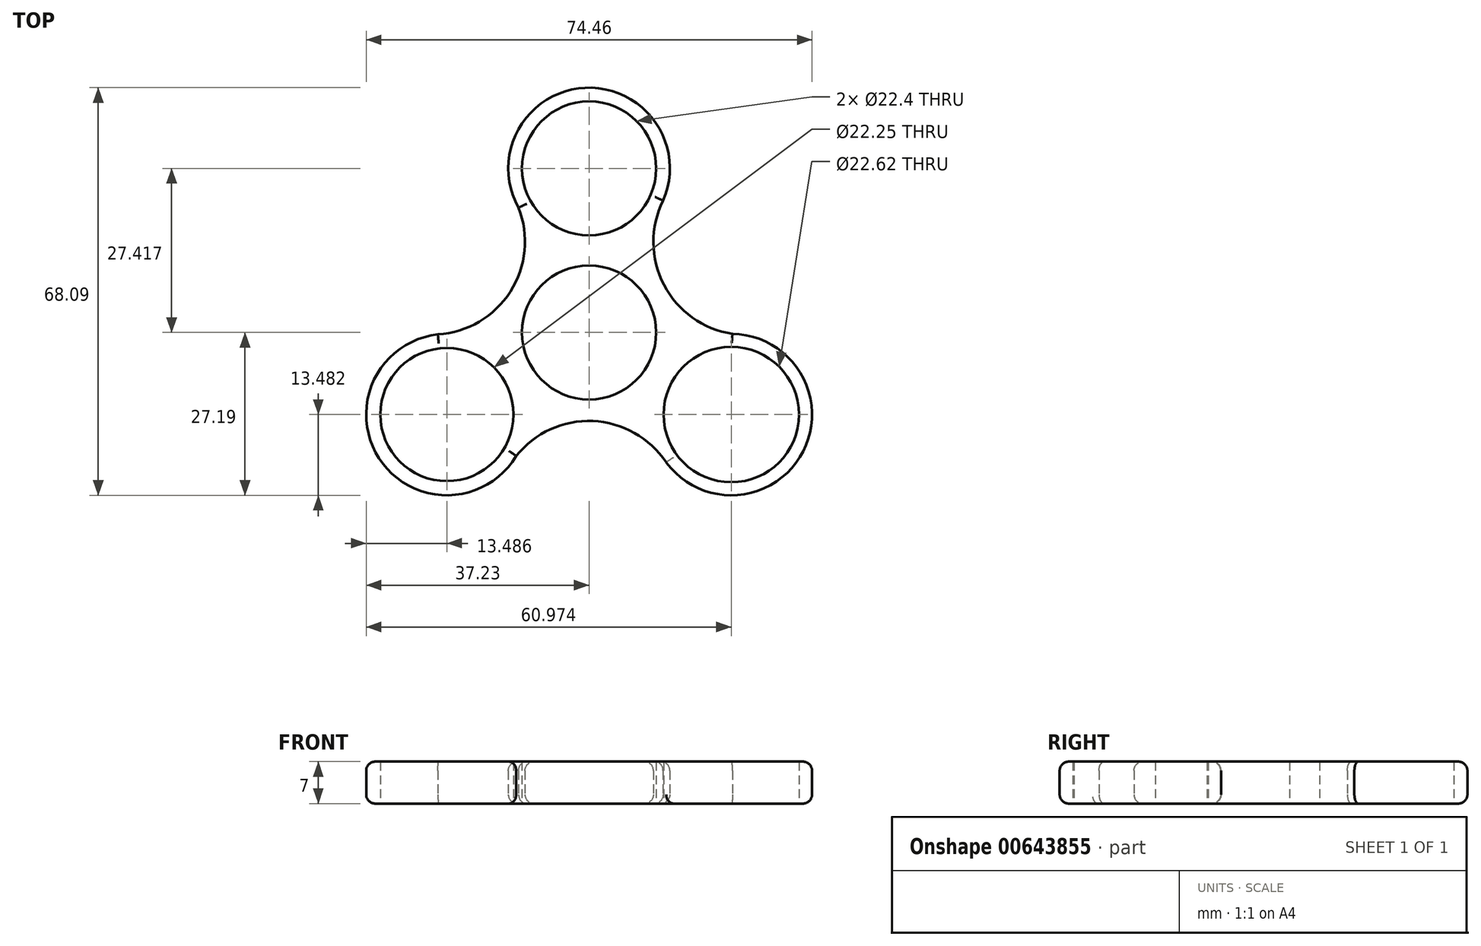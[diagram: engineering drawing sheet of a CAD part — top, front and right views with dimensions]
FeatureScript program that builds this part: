
annotation { "Feature Type Name" : "Feature", "Feature Type Description" : "" }
export const myFeature = defineFeature(function(context is Context, id is Id, definition is map)
    precondition{}
    {
        {
            var Q0;
            Q0=qCreatedBy(makeId("Top.planeOp"),FACE);
            var sketch = newSketch(context, id + "F0", { "sketchPlane" : qUnion([Q0])});
            skCircle(sketch, "E0", {"center": v(0, 0) * mm, "radius": 11.2 * mm});
            skCircle(sketch, "E1", {"center": v(0, 27.42) * mm, "radius": 11.2 * mm});
            skArc(sketch, "E2", {"start": v(12.06, 21.4) * mm, "mid": v(-0.3, 40.9) * mm, "end": v(-11.78, 20.85) * mm});
            skArc(sketch, "E3.1.0", {"start": v(-24.56, -0.25) * mm, "mid": v(-35.26, -20.71) * mm, "end": v(-12.17, -20.62) * mm});
            skArc(sketch, "E3.2.0", {"start": v(12.5, -21.14) * mm, "mid": v(35.57, -20.18) * mm, "end": v(23.95, -0.23) * mm});
            skCircle(sketch, "E4", {"center": v(-23.74, -13.7) * mm, "radius": 11.12 * mm});
            skCircle(sketch, "E5", {"center": v(23.74, -13.7) * mm, "radius": 11.3 * mm});
            skArc(sketch, "E6", {"start": v(12.36, 22.02) * mm, "mid": v(12.5, 7.95) * mm, "end": v(23.95, -0.23) * mm});
            skArc(sketch, "E7.1.0", {"start": v(-25.25, -0.31) * mm, "mid": v(-13.14, 6.85) * mm, "end": v(-11.78, 20.85) * mm});
            skArc(sketch, "E7.2.0", {"start": v(12.9, -21.71) * mm, "mid": v(0.64, -14.8) * mm, "end": v(-12.17, -20.62) * mm});
            skSolve(sketch);
        }
        {
            var Q0;
            Q0=makeQuery(id+"F0.imprint","IMPRINT",FACE,{"disambiguationData":[TD([[makeQuery(id+"F0.imprint","IMPRINT",EDGE,{"derivedFrom":sQuery(id+"F0.wireOp",EDGE,"E0")}),-1.0]])]});
            extrude(context, id + "F1", {"entities" : qUnion([Q0]), "depth" : 7 * mm, "offsetDistance" : 25 * mm});
        }
        {
            var Q0;
            Q0=makeQuery(id+"F1.opExtrude","CAP_EDGE",EDGE,{"disambiguationData":[OSD([sQuery(id+"F0.wireOp",EDGE,"E7.2.0")])],"isStart":false});
            var Q1;
            Q1=makeQuery(id+"F1.opExtrude","CAP_EDGE",EDGE,{"disambiguationData":[OSD([sQuery(id+"F0.wireOp",EDGE,"E7.2.0")])],"isStart":true});
            var Q2;
            Q2=makeQuery(id+"F1.opExtrude","CAP_EDGE",EDGE,{"disambiguationData":[OSD([sQuery(id+"F0.wireOp",EDGE,"E3.1.0")])],"isStart":false});
            var Q3;
            Q3=makeQuery(id+"F1.opExtrude","CAP_EDGE",EDGE,{"disambiguationData":[OSD([sQuery(id+"F0.wireOp",EDGE,"E7.1.0")])],"isStart":false});
            var Q4;
            Q4=makeQuery(id+"F1.opExtrude","CAP_EDGE",EDGE,{"disambiguationData":[OSD([sQuery(id+"F0.wireOp",EDGE,"E2")])],"isStart":false});
            var Q5;
            Q5=makeQuery(id+"F1.opExtrude","CAP_EDGE",EDGE,{"disambiguationData":[OSD([sQuery(id+"F0.wireOp",EDGE,"E6")])],"isStart":false});
            var Q6;
            Q6=makeQuery(id+"F1.opExtrude","CAP_EDGE",EDGE,{"disambiguationData":[OSD([sQuery(id+"F0.wireOp",EDGE,"E3.2.0")])],"isStart":false});
            fillet(context, id + "F2", {"entities" : qUnion([Q0, Q1, Q2, Q3, Q4, Q5, Q6]), "radius" : 1.5 * mm, "tangentPropagation" : true, "allowEdgeOverflow" : false});
        }
        {
            var Q0;
            Q0=makeQuery(id+"F1.opExtrude","CAP_EDGE",EDGE,{"disambiguationData":[OSD([sQuery(id+"F0.wireOp",EDGE,"E3.1.0")])],"isStart":true});
            var Q1;
            Q1=makeQuery(id+"F1.opExtrude","CAP_EDGE",EDGE,{"disambiguationData":[OSD([sQuery(id+"F0.wireOp",EDGE,"E3.2.0")])],"isStart":true});
            var Q2;
            Q2=makeQuery(id+"F1.opExtrude","CAP_EDGE",EDGE,{"disambiguationData":[OSD([sQuery(id+"F0.wireOp",EDGE,"E6")])],"isStart":true});
            var Q3;
            Q3=makeQuery(id+"F1.opExtrude","CAP_EDGE",EDGE,{"disambiguationData":[OSD([sQuery(id+"F0.wireOp",EDGE,"E2")])],"isStart":true});
            var Q4;
            Q4=makeQuery(id+"F1.opExtrude","CAP_EDGE",EDGE,{"disambiguationData":[OSD([sQuery(id+"F0.wireOp",EDGE,"E7.1.0")])],"isStart":true});
            fillet(context, id + "F3", {"entities" : qUnion([Q0, Q1, Q2, Q3, Q4]), "radius" : 1.5 * mm, "tangentPropagation" : true, "allowEdgeOverflow" : false});
        }
    });
